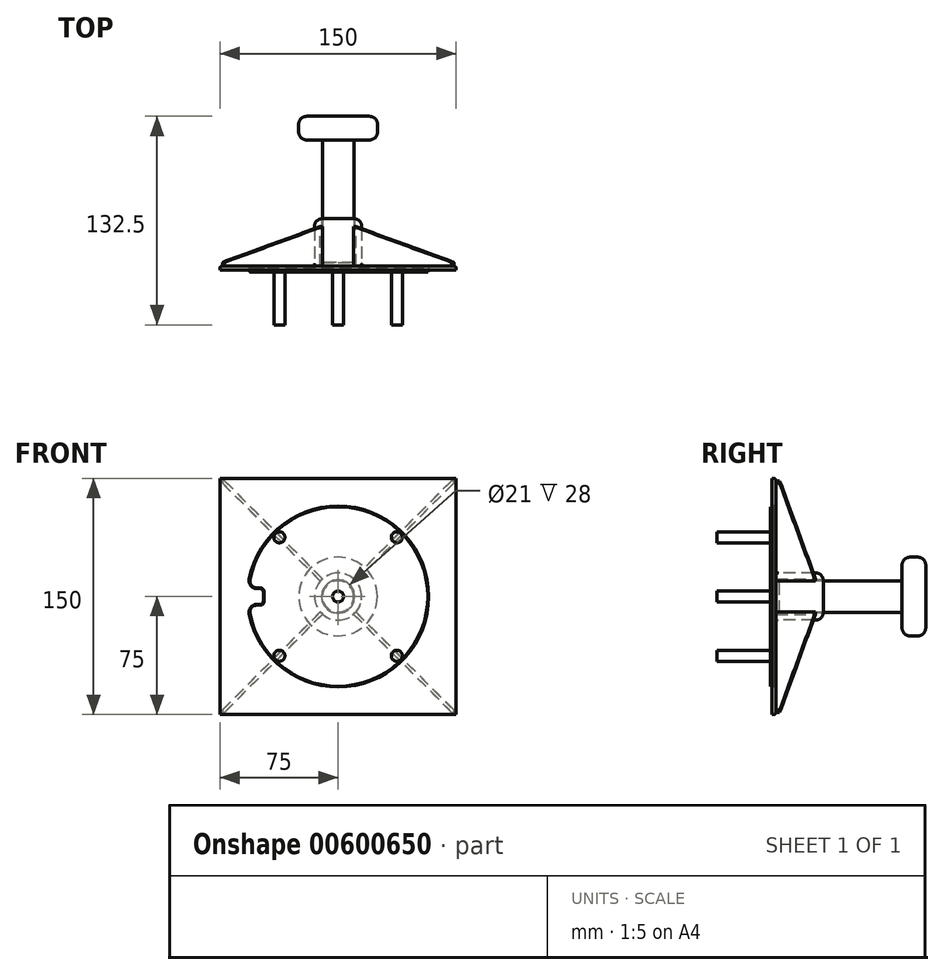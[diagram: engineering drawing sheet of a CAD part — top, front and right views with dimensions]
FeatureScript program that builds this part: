
annotation { "Feature Type Name" : "Feature", "Feature Type Description" : "" }
export const myFeature = defineFeature(function(context is Context, id is Id, definition is map)
    precondition{}
    {
        {
            var Q0;
            Q0=qCreatedBy(makeId("Front.planeOp"),FACE);
            var sketch = newSketch(context, id + "F0", { "sketchPlane" : qUnion([Q0])});
            skLineSegment(sketch, "E0.bottom", {"start": v(75, 75) * mm, "end": v(-75, 75) * mm});
            skLineSegment(sketch, "E0.top", {"start": v(75, -75) * mm, "end": v(-75, -75) * mm});
            skLineSegment(sketch, "E0.left", {"start": v(75, 75) * mm, "end": v(75, -75) * mm});
            skLineSegment(sketch, "E0.right", {"start": v(-75, 75) * mm, "end": v(-75, -75) * mm});
            skPoint(sketch, "E0.middle", {"position": v(0, 0) * mm});
            skSolve(sketch);
        }
        {
            var Q0;
            Q0 = qSketchRegion(id + "F0", true);
            extrude(context, id + "F1", {"entities" : qUnion([Q0]), "depth" : 2.5 * mm, "offsetDistance" : 25 * mm});
        }
        {
            var Q0;
            Q0=makeQuery(id+"F1.opExtrude","CAP_FACE",FACE,{"disambiguationData":[OSD([sQuery(id+"F0.wireOp",EDGE,"E0.bottom"),sQuery(id+"F0.wireOp",EDGE,"E0.top"),sQuery(id+"F0.wireOp",EDGE,"E0.left"),sQuery(id+"F0.wireOp",EDGE,"E0.right")])],"isStart":true});
            var sketch = newSketch(context, id + "F2", { "sketchPlane" : qUnion([Q0])});
            skCircle(sketch, "E1", {"center": v(0, 0) * mm, "radius": 15 * mm});
            skSolve(sketch);
        }
        {
            var Q0;
            Q0 = qSketchRegion(id + "F2", true);
            extrude(context, id + "F3", {"entities" : qUnion([Q0]), "operationType" : NewBodyOperationType.ADD, "depth" : 30 * mm, "offsetDistance" : 25 * mm});
        }
        {
            var Q0;
            Q0=makeQuery(id+"F3.opExtrude","CAP_FACE",FACE,{"disambiguationData":[OSD([sQuery(id+"F2.wireOp",EDGE,"E1")])],"isStart":false});
            var Q1;
            Q1=makeQuery(id+"F1.opExtrude","CAP_FACE",FACE,{"disambiguationData":[OSD([sQuery(id+"F0.wireOp",EDGE,"E0.bottom"),sQuery(id+"F0.wireOp",EDGE,"E0.top"),sQuery(id+"F0.wireOp",EDGE,"E0.left"),sQuery(id+"F0.wireOp",EDGE,"E0.right")])],"isStart":true});
            shell(context, id + "F4", {"entities" : qUnion([Q0, Q1]), "thickness" : 4.5 * mm});
        }
        {
            var Q0;
            Q0=makeQuery(id+"F1.opExtrude","CAP_FACE",FACE,{"disambiguationData":[OSD([sQuery(id+"F0.wireOp",EDGE,"E0.bottom"),sQuery(id+"F0.wireOp",EDGE,"E0.top"),sQuery(id+"F0.wireOp",EDGE,"E0.left"),sQuery(id+"F0.wireOp",EDGE,"E0.right")])],"isStart":false});
            var sketch = newSketch(context, id + "F5", { "sketchPlane" : qUnion([Q0])});
            skCircle(sketch, "E2", {"center": v(-37.3, -37.61) * mm, "radius": 3.5 * mm});
            skCircle(sketch, "E3.MirrorC", {"center": v(37.3, -37.61) * mm, "radius": 3.5 * mm});
            skCircle(sketch, "E4.MirrorC", {"center": v(-37.3, 37.61) * mm, "radius": 3.5 * mm});
            skCircle(sketch, "E5.MirrorC", {"center": v(37.3, 37.61) * mm, "radius": 3.5 * mm});
            skSolve(sketch);
        }
        {
            var Q0;
            Q0 = qSketchRegion(id + "F5", true);
            extrude(context, id + "F6", {"entities" : qUnion([Q0]), "operationType" : NewBodyOperationType.ADD, "depth" : 35 * mm, "offsetDistance" : 25 * mm});
        }
        {
            var Q0;
            Q0=makeQuery(id+"F1.opExtrude","CAP_FACE",FACE,{"disambiguationData":[OSD([sQuery(id+"F0.wireOp",EDGE,"E0.bottom"),sQuery(id+"F0.wireOp",EDGE,"E0.top"),sQuery(id+"F0.wireOp",EDGE,"E0.left"),sQuery(id+"F0.wireOp",EDGE,"E0.right")])],"isStart":true});
            fillet(context, id + "F7", {"entities" : qUnion([Q0]), "radius" : 1.5 * mm, "tangentPropagation" : true, "allowEdgeOverflow" : false});
        }
        {
            var Q0;
            Q0=makeQuery(id+"F3.opExtrude","CAP_EDGE",EDGE,{"disambiguationData":[OSD([sQuery(id+"F2.wireOp",EDGE,"E1")])],"isStart":false});
            fillet(context, id + "F8", {"entities" : qUnion([Q0]), "radius" : 5 * mm, "tangentPropagation" : true, "allowEdgeOverflow" : false});
        }
        {
            var Q0;
            Q0=makeQuery(id+"F1.opExtrude","CAP_FACE",FACE,{"disambiguationData":[OSD([sQuery(id+"F0.wireOp",EDGE,"E0.bottom"),sQuery(id+"F0.wireOp",EDGE,"E0.top"),sQuery(id+"F0.wireOp",EDGE,"E0.left"),sQuery(id+"F0.wireOp",EDGE,"E0.right")])],"isStart":true});
            var sketch = newSketch(context, id + "F9", { "sketchPlane" : qUnion([Q0])});
            skLineSegment(sketch, "E6", {"start": v(73.5, -72.09) * mm, "end": v(11.3, -9.88) * mm});
            skLineSegment(sketch, "E7", {"start": v(73.5, -73.5) * mm, "end": v(73.5, -72.09) * mm});
            skLineSegment(sketch, "E8", {"start": v(72.09, -73.5) * mm, "end": v(9.88, -11.3) * mm});
            skLineSegment(sketch, "E9", {"start": v(72.09, -73.5) * mm, "end": v(73.5, -73.5) * mm});
            skArc(sketch, "E10", {"start": v(9.88, -11.3) * mm, "mid": v(10.6, -10.6) * mm, "end": v(11.3, -9.88) * mm});
            skLineSegment(sketch, "E11", {"start": v(10.6, -10.6) * mm, "end": v(73.5, -73.5) * mm, "construction": true});
            skLineSegment(sketch, "E12.MirrorCS", {"start": v(73.5, 73.5) * mm, "end": v(73.5, 72.09) * mm});
            skLineSegment(sketch, "E13.MirrorCS", {"start": v(72.09, 73.5) * mm, "end": v(73.5, 73.5) * mm});
            skLineSegment(sketch, "E14.MirrorCS", {"start": v(-72.09, 73.5) * mm, "end": v(-73.5, 73.5) * mm});
            skLineSegment(sketch, "E15.MirrorCS", {"start": v(-72.09, -73.5) * mm, "end": v(-73.5, -73.5) * mm});
            skLineSegment(sketch, "E16.MirrorCS", {"start": v(-73.5, -73.5) * mm, "end": v(-73.5, -72.09) * mm});
            skSolve(sketch);
        }
        {
            var Q0;
            {var subQ7=sQuery(id+"F9.wireOp",EDGE,"E7");Q0=makeQuery(id+"F9.imprint","IMPRINT",FACE,{"disambiguationData":[TD([[makeQuery(id+"F9.imprint","IMPRINT",EDGE,{"derivedFrom":subQ7}),1.0]])]});}
            var Q1;
            {var subQ0=sQuery(id+"F9.wireOp",EDGE,"E10");Q1=makeQuery(id+"F9.imprint","IMPRINT",FACE,{"disambiguationData":[TD([[makeQuery(id+"F9.imprint","IMPRINT",EDGE,{"derivedFrom":subQ0}),-1.0]])]});}
            extrude(context, id + "F10", {"entities" : qUnion([Q0, Q1]), "depth" : 25 * mm, "offsetDistance" : 25 * mm, "hasDraft" : true, "draftAngle" : 0 * degree});
        }
        {
            var Q0;
            Q0=makeQuery(id+"F1.opExtrude","CAP_FACE",FACE,{"disambiguationData":[OSD([sQuery(id+"F0.wireOp",EDGE,"E0.bottom"),sQuery(id+"F0.wireOp",EDGE,"E0.top"),sQuery(id+"F0.wireOp",EDGE,"E0.left"),sQuery(id+"F0.wireOp",EDGE,"E0.right")])],"isStart":false});
            var sketch = newSketch(context, id + "F11", { "sketchPlane" : qUnion([Q0])});
            skCircle(sketch, "E17", {"center": v(0, 0) * mm, "radius": 3.5 * mm});
            skSolve(sketch);
        }
        {
            var Q0;
            Q0 = qSketchRegion(id + "F11", true);
            extrude(context, id + "F12", {"entities" : qUnion([Q0]), "operationType" : NewBodyOperationType.ADD, "depth" : 35 * mm, "offsetDistance" : 25 * mm});
        }
        {
            var Q0;
            Q0=makeQuery(id+"F10.opExtrude","SWEPT_FACE",FACE,{"disambiguationData":[OSD([sQuery(id+"F9.wireOp",EDGE,"E6")])]});
            var Q1;
            Q1=makeQuery(id+"F10.opExtrude","SWEPT_FACE",FACE,{"disambiguationData":[OSD([sQuery(id+"F9.wireOp",EDGE,"E8")])]});
            cPlane(context, id + "F13", {"entities" : qUnion([Q0, Q1]), "cplaneType" : CPlaneType.MID_PLANE, "offset" : 25 * mm, "width" : 150 * mm, "height" : 150 * mm});
        }
        {
            var Q0;
            Q0=qCreatedBy(id+"F13.planeOp",FACE);
            var sketch = newSketch(context, id + "F14", { "sketchPlane" : qUnion([Q0])});
            skLineSegment(sketch, "E18", {"start": v(-25, -103.94) * mm, "end": v(-25, -15) * mm});
            skLineSegment(sketch, "E19", {"start": v(-25, -15) * mm, "end": v(-2, -103.94) * mm});
            skLineSegment(sketch, "E20", {"start": v(-2, -103.94) * mm, "end": v(-25, -103.94) * mm});
            skSolve(sketch);
        }
        {
            var Q0;
            Q0 = qSketchRegion(id + "F14", true);
            var Q1;
            Q1=makeQuery(id+"F3.opExtrude","SWEPT_FACE",FACE,{"disambiguationData":[OSD([sQuery(id+"F2.wireOp",EDGE,"E1")])]});
            revolve(context, id + "F15", {"operationType" : NewBodyOperationType.REMOVE, "entities" : qUnion([Q0]), "axis" : qUnion([Q1]), "revolveType" : RevolveType.FULL, "oppositeDirection" : true});
        }
        {
            var Q0;
            Q0=makeQuery(id+"F10.opExtrude","SWEPT_BODY",BODY,{"disambiguationData":[OSD([sQuery(id+"F9.wireOp",EDGE,"E6"),sQuery(id+"F9.wireOp",EDGE,"E7"),sQuery(id+"F9.wireOp",EDGE,"E8"),sQuery(id+"F9.wireOp",EDGE,"E9"),sQuery(id+"F9.wireOp",EDGE,"E10")])]});
            var Q1;
            {var subQ0=sQuery(id+"F2.wireOp",EDGE,"E1");Q1=makeQuery(id+"F15.boolean.opBoolean","SPLIT",FACE,{"disambiguationData":[TD([makeQuery(id+"F7.opFillet","BLEND_FACE",FACE,{"disambiguationData":[OSD([subQ0])]})])],"derivedFrom":makeQuery(id+"F3.opExtrude","SWEPT_FACE",FACE,{"disambiguationData":[OSD([subQ0])]})});}
            circularPattern(context, id + "F16", {"entities" : qUnion([Q0]), "axis" : qUnion([Q1]), "angle" : 360 * degree, "instanceCount" : 4, "equalSpace" : true});
        }
        {
            var Q0;
            Q0=makeQuery(id+"F11.imprint","IMPRINT",FACE,{"disambiguationData":[TD([[makeQuery(id+"F11.imprint","IMPRINT",EDGE,{"derivedFrom":sQuery(id+"F11.wireOp",EDGE,"E17")}),-1.0]])]});
            var sketch = newSketch(context, id + "F17", { "sketchPlane" : qUnion([Q0])});
            skArc(sketch, "E21", {"start": v(-56.45, -10.95) * mm, "mid": v(57.5, 0) * mm, "end": v(-56.45, 10.95) * mm});
            skLineSegment(sketch, "E22", {"start": v(-51.54, -5) * mm, "end": v(-49.5, -5) * mm});
            skLineSegment(sketch, "E23", {"start": v(-47.5, -3) * mm, "end": v(-47.5, 3) * mm});
            skLineSegment(sketch, "E24", {"start": v(-49.5, 5) * mm, "end": v(-51.54, 5) * mm});
            skPoint(sketch, "E25.visualSharp", {"position": v(-57.28, -5) * mm});
            skArc(sketch, "E25.filletArc", {"start": v(-51.54, -5) * mm, "mid": v(-55.4, -6.82) * mm, "end": v(-56.45, -10.95) * mm});
            skPoint(sketch, "E26.visualSharp", {"position": v(-47.5, -5) * mm});
            skArc(sketch, "E26.filletArc", {"start": v(-49.5, -5) * mm, "mid": v(-48.09, -4.41) * mm, "end": v(-47.5, -3) * mm});
            skPoint(sketch, "E27.visualSharp", {"position": v(-47.5, 5) * mm});
            skArc(sketch, "E27.filletArc", {"start": v(-47.5, 3) * mm, "mid": v(-48.09, 4.41) * mm, "end": v(-49.5, 5) * mm});
            skPoint(sketch, "E28.visualSharp", {"position": v(-57.28, 5) * mm});
            skArc(sketch, "E28.filletArc", {"start": v(-56.45, 10.95) * mm, "mid": v(-55.4, 6.82) * mm, "end": v(-51.54, 5) * mm});
            skSolve(sketch);
        }
        {
            var Q0;
            Q0 = qSketchRegion(id + "F17", true);
            extrude(context, id + "F18", {"entities" : qUnion([Q0]), "operationType" : NewBodyOperationType.REMOVE, "oppositeDirection" : true, "depth" : 1.25 * mm, "offsetDistance" : 25 * mm});
        }
        {
            var Q0;
            Q0=makeQuery(id+"F11.imprint","IMPRINT",FACE,{"disambiguationData":[TD([[makeQuery(id+"F11.imprint","IMPRINT",EDGE,{"derivedFrom":sQuery(id+"F11.wireOp",EDGE,"E17")}),-1.0]])]});
            var sketch = newSketch(context, id + "F19", { "sketchPlane" : qUnion([Q0])});
            skArc(sketch, "E29", {"start": v(-55.98, -10.73) * mm, "mid": v(57, 0) * mm, "end": v(-55.98, 10.73) * mm});
            skLineSegment(sketch, "E30", {"start": v(-51.66, -5.5) * mm, "end": v(-49.4, -5.5) * mm});
            skLineSegment(sketch, "E31", {"start": v(-47, -3.1) * mm, "end": v(-47, 3.1) * mm});
            skLineSegment(sketch, "E32", {"start": v(-49.4, 5.5) * mm, "end": v(-51.66, 5.5) * mm});
            skPoint(sketch, "E33.visualSharp", {"position": v(-56.73, -5.5) * mm});
            skArc(sketch, "E33.filletArc", {"start": v(-51.66, -5.5) * mm, "mid": v(-55.05, -7.1) * mm, "end": v(-55.98, -10.73) * mm});
            skPoint(sketch, "E34.visualSharp", {"position": v(-56.73, 5.5) * mm});
            skArc(sketch, "E34.filletArc", {"start": v(-55.98, 10.73) * mm, "mid": v(-55.05, 7.1) * mm, "end": v(-51.66, 5.5) * mm});
            skPoint(sketch, "E35.visualSharp", {"position": v(-47, 5.5) * mm});
            skArc(sketch, "E35.filletArc", {"start": v(-47, 3.1) * mm, "mid": v(-47.7, 4.8) * mm, "end": v(-49.4, 5.5) * mm});
            skPoint(sketch, "E36.visualSharp", {"position": v(-47, -5.5) * mm});
            skArc(sketch, "E36.filletArc", {"start": v(-49.4, -5.5) * mm, "mid": v(-47.7, -4.8) * mm, "end": v(-47, -3.1) * mm});
            skSolve(sketch);
        }
        {
            var Q0;
            Q0 = qSketchRegion(id + "F19", true);
            extrude(context, id + "F20", {"entities" : qUnion([Q0]), "depth" : 1.25 * mm, "offsetDistance" : 25 * mm});
        }
        {
            var Q0;
            Q0=makeQuery(id+"F0.imprint","IMPRINT",FACE,{"disambiguationData":[TD([[makeQuery(id+"F0.imprint","IMPRINT",EDGE,{"derivedFrom":sQuery(id+"F0.wireOp",EDGE,"E0.bottom")}),1.0]])]});
            var sketch = newSketch(context, id + "F21", { "sketchPlane" : qUnion([Q0])});
            skCircle(sketch, "E37", {"center": v(0, 0) * mm, "radius": 10 * mm});
            skSolve(sketch);
        }
        {
            var Q0;
            Q0 = qSketchRegion(id + "F21", true);
            extrude(context, id + "F22", {"entities" : qUnion([Q0]), "operationType" : NewBodyOperationType.ADD, "oppositeDirection" : true, "depth" : 80 * mm, "offsetDistance" : 25 * mm});
        }
        {
            var Q0;
            Q0=makeQuery(id+"F22.opExtrude","CAP_FACE",FACE,{"disambiguationData":[OSD([sQuery(id+"F21.wireOp",EDGE,"E37")])],"isStart":false});
            var sketch = newSketch(context, id + "F23", { "sketchPlane" : qUnion([Q0])});
            skCircle(sketch, "E38", {"center": v(0, 0) * mm, "radius": 25 * mm});
            skSolve(sketch);
        }
        {
            var Q0;
            Q0 = qSketchRegion(id + "F23", true);
            extrude(context, id + "F24", {"entities" : qUnion([Q0]), "operationType" : NewBodyOperationType.ADD, "depth" : 15 * mm, "offsetDistance" : 25 * mm});
        }
        {
            var Q0;
            Q0=makeQuery(id+"F24.opExtrude","CAP_FACE",FACE,{"disambiguationData":[OSD([sQuery(id+"F23.wireOp",EDGE,"E38")])],"isStart":false});
            var Q1;
            Q1=makeQuery(id+"F24.opExtrude","CAP_EDGE",EDGE,{"disambiguationData":[OSD([sQuery(id+"F23.wireOp",EDGE,"E38")])],"isStart":true});
            fillet(context, id + "F25", {"entities" : qUnion([Q0, Q1]), "radius" : 5 * mm, "tangentPropagation" : true, "allowEdgeOverflow" : false});
        }
    });
